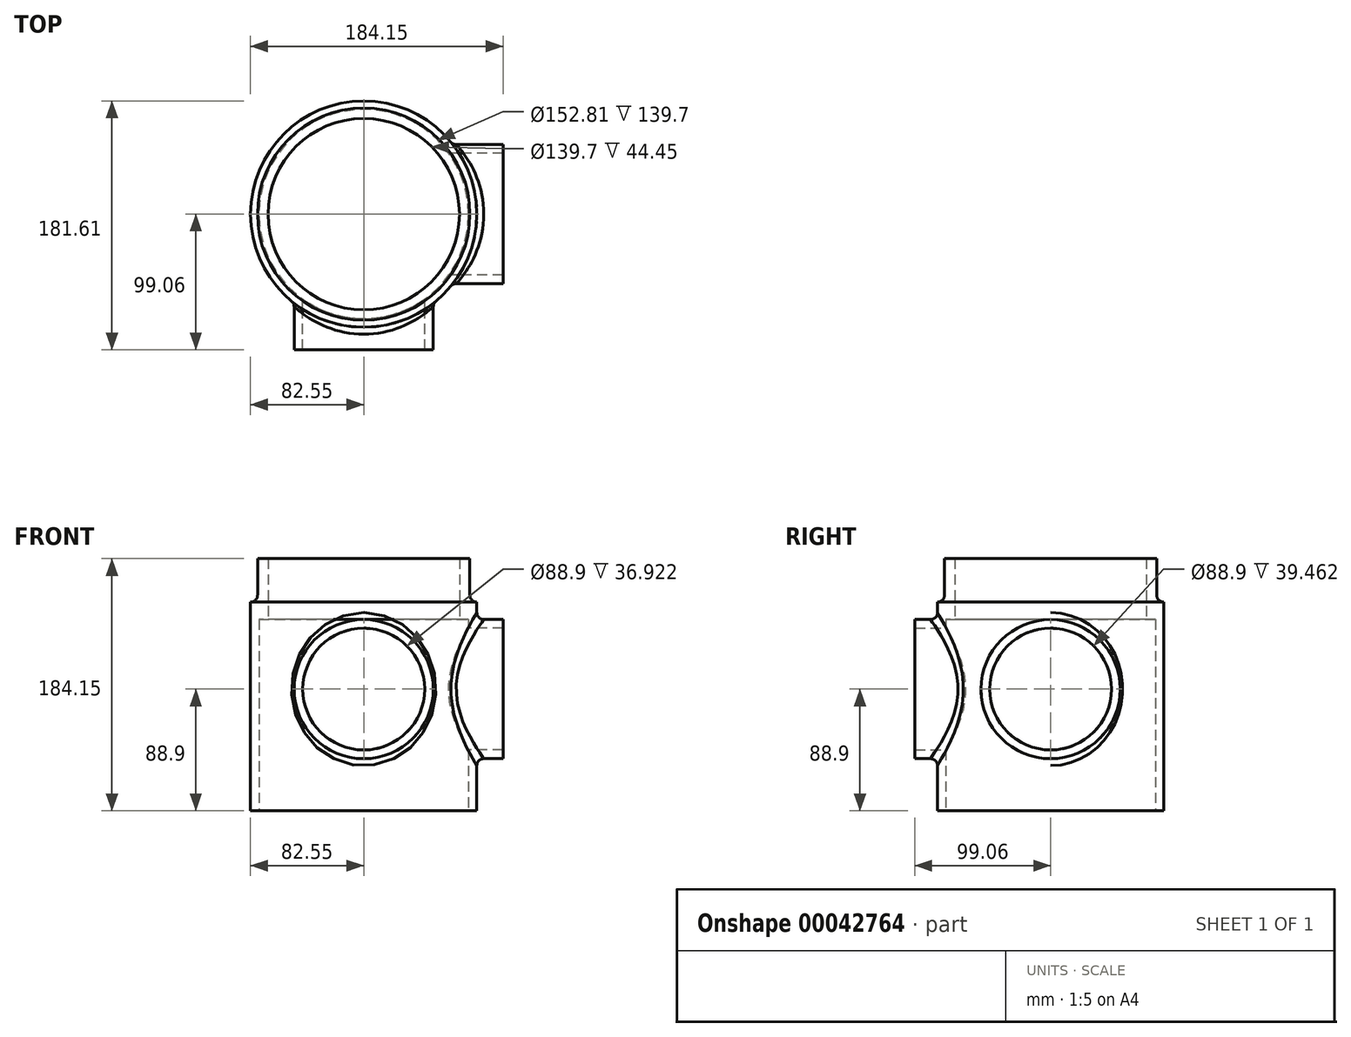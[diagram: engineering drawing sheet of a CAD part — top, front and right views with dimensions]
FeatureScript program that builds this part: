
annotation { "Feature Type Name" : "Feature", "Feature Type Description" : "" }
export const myFeature = defineFeature(function(context is Context, id is Id, definition is map)
    precondition{}
    {
        {
            var Q0;
            Q0=qCreatedBy(makeId("Top.planeOp"),FACE);
            var sketch = newSketch(context, id + "F0", { "sketchPlane" : qUnion([Q0])});
            skCircle(sketch, "E0", {"center": v(0, 0) * mm, "radius": 76.4 * mm});
            skCircle(sketch, "E1", {"center": v(0, 0) * mm, "radius": 82.55 * mm});
            skSolve(sketch);
        }
        {
            var Q0;
            Q0=makeQuery(id+"F0.imprint","IMPRINT",FACE,{"disambiguationData":[TD([[makeQuery(id+"F0.imprint","IMPRINT",EDGE,{"derivedFrom":sQuery(id+"F0.wireOp",EDGE,"E0")}),-1.0]])]});
            extrude(context, id + "F1", {"entities" : qUnion([Q0]), "depth" : 63.5 * mm, "hasSecondDirection" : true, "secondDirectionOppositeDirection" : true, "secondDirectionDepth" : 88.9 * mm});
        }
        {
            var Q0;
            Q0=qCreatedBy(makeId("Front.planeOp"),FACE);
            var sketch = newSketch(context, id + "F2", { "sketchPlane" : qUnion([Q0])});
            skCircle(sketch, "E2", {"center": v(0, 0) * mm, "radius": 50.8 * mm});
            skCircle(sketch, "E3", {"center": v(0, 0) * mm, "radius": 44.45 * mm});
            skSolve(sketch);
        }
        {
            var Q0;
            Q0 = qSketchRegion(id + "F2", true);
            extrude(context, id + "F3", {"entities" : qUnion([Q0]), "operationType" : NewBodyOperationType.ADD, "depth" : 99.06 * mm});
        }
        {
            var Q0;
            Q0=makeQuery(id+"F2.imprint","IMPRINT",FACE,{"disambiguationData":[TD([[makeQuery(id+"F2.imprint","IMPRINT",EDGE,{"derivedFrom":sQuery(id+"F2.wireOp",EDGE,"E3")}),1.0]])]});
            extrude(context, id + "F4", {"entities" : qUnion([Q0]), "operationType" : NewBodyOperationType.REMOVE, "depth" : 127 * mm});
        }
        {
            var Q0;
            Q0=qCreatedBy(makeId("Right.planeOp"),FACE);
            var sketch = newSketch(context, id + "F5", { "sketchPlane" : qUnion([Q0])});
            skCircle(sketch, "E4", {"center": v(0, 0) * mm, "radius": 50.8 * mm});
            skCircle(sketch, "E5", {"center": v(0, 0) * mm, "radius": 44.45 * mm});
            skSolve(sketch);
        }
        {
            var Q0;
            Q0=makeQuery(id+"F5.imprint","IMPRINT",FACE,{"disambiguationData":[TD([[makeQuery(id+"F5.imprint","IMPRINT",EDGE,{"derivedFrom":sQuery(id+"F5.wireOp",EDGE,"E4")}),1.0]])]});
            extrude(context, id + "F6", {"entities" : qUnion([Q0]), "operationType" : NewBodyOperationType.ADD, "depth" : 101.6 * mm});
        }
        {
            var Q0;
            Q0=makeQuery(id+"F5.imprint","IMPRINT",FACE,{"disambiguationData":[TD([[makeQuery(id+"F5.imprint","IMPRINT",EDGE,{"derivedFrom":sQuery(id+"F5.wireOp",EDGE,"E5")}),1.0]])]});
            extrude(context, id + "F7", {"entities" : qUnion([Q0]), "operationType" : NewBodyOperationType.REMOVE, "depth" : 101.6 * mm});
        }
        {
            var Q0;
            Q0=makeQuery(id+"F0.imprint","IMPRINT",FACE,{"disambiguationData":[TD([[makeQuery(id+"F0.imprint","IMPRINT",EDGE,{"derivedFrom":sQuery(id+"F0.wireOp",EDGE,"E0")}),1.0]])]});
            extrude(context, id + "F8", {"entities" : qUnion([Q0]), "operationType" : NewBodyOperationType.REMOVE, "oppositeDirection" : true, "depth" : 203.2 * mm, "hasSecondDirection" : true, "secondDirectionOppositeDirection" : false, "secondDirectionDepth" : 203.2 * mm});
        }
        {
            var Q0;
            Q0=qCreatedBy(makeId("Top.planeOp"),FACE);
            cPlane(context, id + "F9", {"entities" : qUnion([Q0]), "cplaneType" : CPlaneType.OFFSET, "offset" : 57.15 * mm, "width" : 152.4 * mm, "height" : 152.4 * mm});
        }
        {
            var Q0;
            Q0=qCreatedBy(id+"F9.planeOp",FACE);
            var sketch = newSketch(context, id + "F10", { "sketchPlane" : qUnion([Q0])});
            skCircle(sketch, "E6", {"center": v(0, 0) * mm, "radius": 77.47 * mm});
            skCircle(sketch, "E7", {"center": v(0, 0) * mm, "radius": 69.85 * mm});
            skSolve(sketch);
        }
        {
            var Q0;
            Q0=makeQuery(id+"F10.imprint","IMPRINT",FACE,{"disambiguationData":[TD([[makeQuery(id+"F10.imprint","IMPRINT",EDGE,{"derivedFrom":sQuery(id+"F10.wireOp",EDGE,"E6")}),1.0]])]});
            extrude(context, id + "F11", {"entities" : qUnion([Q0]), "operationType" : NewBodyOperationType.ADD, "depth" : 38.1 * mm, "hasSecondDirection" : true, "secondDirectionOppositeDirection" : true, "secondDirectionDepth" : 6.35 * mm});
        }
        {
            var Q0;
            Q0=makeQuery(id+"F3.boolean.opBoolean","INTERSECT",EDGE,{"disambiguationData":[OD(1.0)],"derivedFrom":[makeQuery(id+"F1.opExtrude","SWEPT_FACE",FACE,{"disambiguationData":[OSD([sQuery(id+"F0.wireOp",EDGE,"E1")])]}),makeQuery(id+"F3.opExtrude","SWEPT_FACE",FACE,{"disambiguationData":[OSD([sQuery(id+"F2.wireOp",EDGE,"E2")])]})]});
            var Q1;
            Q1=makeQuery(id+"F3.boolean.opBoolean","INTERSECT",EDGE,{"disambiguationData":[OD(0.0)],"derivedFrom":[makeQuery(id+"F1.opExtrude","SWEPT_FACE",FACE,{"disambiguationData":[OSD([sQuery(id+"F0.wireOp",EDGE,"E1")])]}),makeQuery(id+"F3.opExtrude","SWEPT_FACE",FACE,{"disambiguationData":[OSD([sQuery(id+"F2.wireOp",EDGE,"E2")])]})]});
            fillet(context, id + "F12", {"entities" : qUnion([Q0, Q1]), "radius" : 5.08 * mm, "tangentPropagation" : true, "allowEdgeOverflow" : false});
        }
        {
            var Q0;
            Q0=makeQuery(id+"F11.boolean.opBoolean","INTERSECT",EDGE,{"derivedFrom":[makeQuery(id+"F1.opExtrude","CAP_FACE",FACE,{"disambiguationData":[OSD([sQuery(id+"F0.wireOp",EDGE,"E0"),sQuery(id+"F0.wireOp",EDGE,"E1")])],"isStart":false}),makeQuery(id+"F11.opExtrude","SWEPT_FACE",FACE,{"disambiguationData":[OSD([sQuery(id+"F10.wireOp",EDGE,"E6")])]})]});
            fillet(context, id + "F13", {"entities" : qUnion([Q0]), "radius" : 5.08 * mm, "tangentPropagation" : true, "allowEdgeOverflow" : false});
        }
        {
            var Q0;
            {var subQ0=sQuery(id+"F0.wireOp",EDGE,"E1");Q0=makeQuery(id+"F6.boolean.opBoolean","INTERSECT",EDGE,{"derivedFrom":[makeQuery(id+"F3.boolean.opBoolean","SPLIT",FACE,{"disambiguationData":[TD([makeQuery(id+"F3.opExtrude","SWEPT_FACE",FACE,{"disambiguationData":[OSD([sQuery(id+"F2.wireOp",EDGE,"E2")])]})])],"derivedFrom":makeQuery(id+"F1.opExtrude","SWEPT_FACE",FACE,{"disambiguationData":[OSD([subQ0])]})}),makeQuery(id+"F6.opExtrude","SWEPT_FACE",FACE,{"disambiguationData":[OSD([sQuery(id+"F5.wireOp",EDGE,"E4")])]})]});}
            fillet(context, id + "F14", {"entities" : qUnion([Q0]), "radius" : 5.08 * mm, "tangentPropagation" : true, "allowEdgeOverflow" : false});
        }
    });
